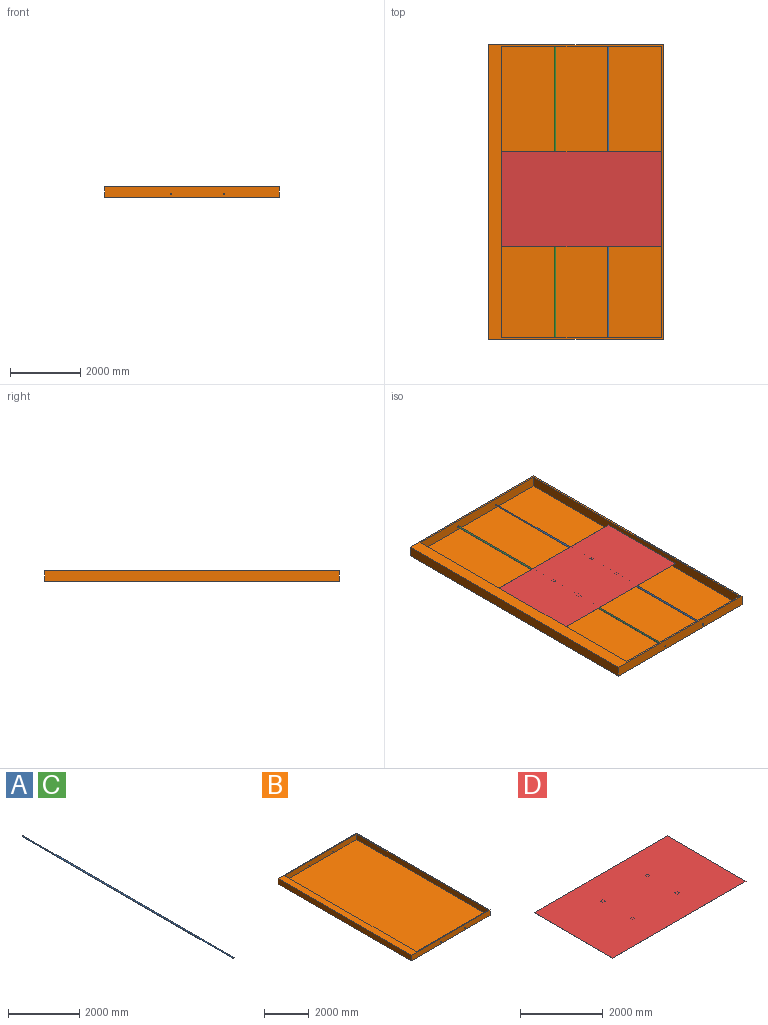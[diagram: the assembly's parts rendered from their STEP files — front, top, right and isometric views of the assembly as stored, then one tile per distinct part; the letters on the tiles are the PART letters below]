
ASSEMBLY  parts=4 mates=7
PART A: 3 faces, bbox 40x8382x40 mm
  f0: cylinder r=20mm len=8382mm, axis (0,1,0), area 1053313.2mm2, adj f1,f2
  f1: plane 40x40mm, normal (0,-1,0), area 1256.6mm2, adj f0
  f2: plane 40x40mm, normal (0,1,0), area 1256.6mm2, adj f0
PART B: 15 faces, bbox 4966x8382x302 mm
  f0: plane 8282x300mm, normal (-1,0,0), area 2484600mm2, adj f1,f7,f8,f9
  f1: plane 4548x300mm, normal (0,1,0), area 1361886.7mm2, adj f0,f2,f8,f9,f13,f14
  f2: plane 8282x300mm, normal (1,0,0), area 2484600mm2, adj f1,f7,f8,f9
  f3: plane 8382x302mm, normal (-1,0,0), area 2531364mm2, adj f4,f6,f8,f10
  f4: plane 4966x302mm, normal (0,-1,0), area 1497218.7mm2, adj f3,f5,f8,f10,f13,f14
  f5: plane 8382x302mm, normal (1,0,0), area 2531364mm2, adj f4,f6,f8,f10
  f6: plane 4966x302mm, normal (0,1,0), area 1497218.7mm2, adj f3,f5,f8,f10,f11,f12
  f7: plane 4548x300mm, normal (0,-1,0), area 1361886.7mm2, adj f0,f2,f8,f9,f11,f12
  f8: plane 8382x4966mm, normal (0,0,1), area 3958476mm2, adj f0,f1,f2,f3,f4,f5,f6,f7
  f9: plane 8282x4548mm, normal (0,0,1), area 37666536mm2, adj f0,f1,f2,f7
  f10: plane 8382x4966mm, normal (0,0,-1), area 41625012mm2, adj f3,f4,f5,f6
  f11: cylinder r=20mm len=50mm, axis (0,-1,0), area 6283.2mm2, adj f6,f7
  f12: cylinder r=20mm len=50mm, axis (0,-1,0), area 6283.2mm2, adj f6,f7
  f13: cylinder r=20mm len=50mm, axis (0,-1,0), area 6283.2mm2, adj f1,f4
  f14: cylinder r=20mm len=50mm, axis (0,-1,0), area 6283.2mm2, adj f1,f4
PART C: same geometry as A
PART D: 30 faces, bbox 4548x2694x82 mm
  f0: plane 4548x2694mm, normal (0,0,-1), area 12226712mm2, adj f1,f2,f3,f4,f6,f7,f8,f9
  f1: plane 4548x2mm, normal (0,1,0), area 9096mm2, adj f0,f2,f4,f5
  f2: plane 2694x2mm, normal (-1,0,0), area 5388mm2, adj f0,f1,f3,f5
  f3: plane 4548x2mm, normal (0,-1,0), area 9096mm2, adj f0,f2,f4,f5
  f4: plane 2694x2mm, normal (1,0,0), area 5388mm2, adj f0,f1,f3,f5
  f5: plane 4548x2694mm, normal (0,0,1), area 12252312mm2, adj f1,f2,f3,f4
  f6: plane 80x80mm, normal (-1,0,0), area 6400mm2, adj f0,f7,f9,f10
  f7: plane 80x80mm, normal (0,1,0), area 5143.4mm2, adj f0,f6,f8,f10,f29
  f8: plane 80x80mm, normal (1,0,0), area 6400mm2, adj f0,f7,f9,f10
  f9: plane 80x80mm, normal (0,-1,0), area 5143.4mm2, adj f0,f6,f8,f10,f29
  f10: plane 80x80mm, normal (0,0,-1), area 6400mm2, adj f6,f7,f8,f9
  f11: plane 80x80mm, normal (-1,0,0), area 6400mm2, adj f0,f12,f14,f15
  f12: plane 80x80mm, normal (0,1,0), area 5143.4mm2, adj f0,f11,f13,f15,f28
  f13: plane 80x80mm, normal (1,0,0), area 6400mm2, adj f0,f12,f14,f15
  f14: plane 80x80mm, normal (0,-1,0), area 5143.4mm2, adj f0,f11,f13,f15,f28
  f15: plane 80x80mm, normal (0,0,-1), area 6400mm2, adj f11,f12,f13,f14
  f16: plane 80x80mm, normal (-1,0,0), area 6400mm2, adj f0,f17,f19,f20
  f17: plane 80x80mm, normal (0,1,0), area 5143.4mm2, adj f0,f16,f18,f20,f27
  f18: plane 80x80mm, normal (1,0,0), area 6400mm2, adj f0,f17,f19,f20
  f19: plane 80x80mm, normal (0,-1,0), area 5143.4mm2, adj f0,f16,f18,f20,f27
  f20: plane 80x80mm, normal (0,0,-1), area 6400mm2, adj f16,f17,f18,f19
  f21: plane 80x80mm, normal (-1,0,0), area 6400mm2, adj f0,f22,f24,f25
  f22: plane 80x80mm, normal (0,1,0), area 5143.4mm2, adj f0,f21,f23,f25,f26
  f23: plane 80x80mm, normal (1,0,0), area 6400mm2, adj f0,f22,f24,f25
  f24: plane 80x80mm, normal (0,-1,0), area 5143.4mm2, adj f0,f21,f23,f25,f26
  f25: plane 80x80mm, normal (0,0,-1), area 6400mm2, adj f21,f22,f23,f24
  f26: cylinder r=20mm len=80mm, axis (0,-1,0), area 10053.1mm2, adj f22,f24
  f27: cylinder r=20mm len=80mm, axis (0,-1,0), area 10053.1mm2, adj f17,f19
  f28: cylinder r=20mm len=80mm, axis (0,-1,0), area 10053.1mm2, adj f12,f14
  f29: cylinder r=20mm len=80mm, axis (0,-1,0), area 10053.1mm2, adj f7,f9
PLACE A t=(3401.18,8371.08,105.71)mm
PLACE B t=(1.18,-10.92,5.71)mm fixed
PLACE C t=(1885.18,8371.08,105.71)mm
PLACE D t=(369.18,2626.84,145.71)mm
MATE slider D.f27 <-> C.f0  axis (0,-1,0) through (1885.18,3466.84,105.71)mm
MATE slider A.f0 <-> D.f26  axis (0,1,0) through (3401.18,8371.08,105.71)mm
MATE parallel D.f1 <-> B.f7  axis (0,1,0) through (2643.18,5320.84,146.71)mm
MATE cylindrical C.f0 <-> B.f12  axis (0,1,0) through (1885.18,4180.08,105.71)mm
MATE planar A.f0 <-> B.f6  axis (0,1,0) through (3401.18,8371.08,105.71)mm
MATE cylindrical A.f0 <-> B.f11  axis (0,-1,0) through (3401.18,-10.92,105.71)mm
MATE planar C.f0 <-> B.f6  axis (0,1,0) through (1885.18,8371.08,105.71)mm
